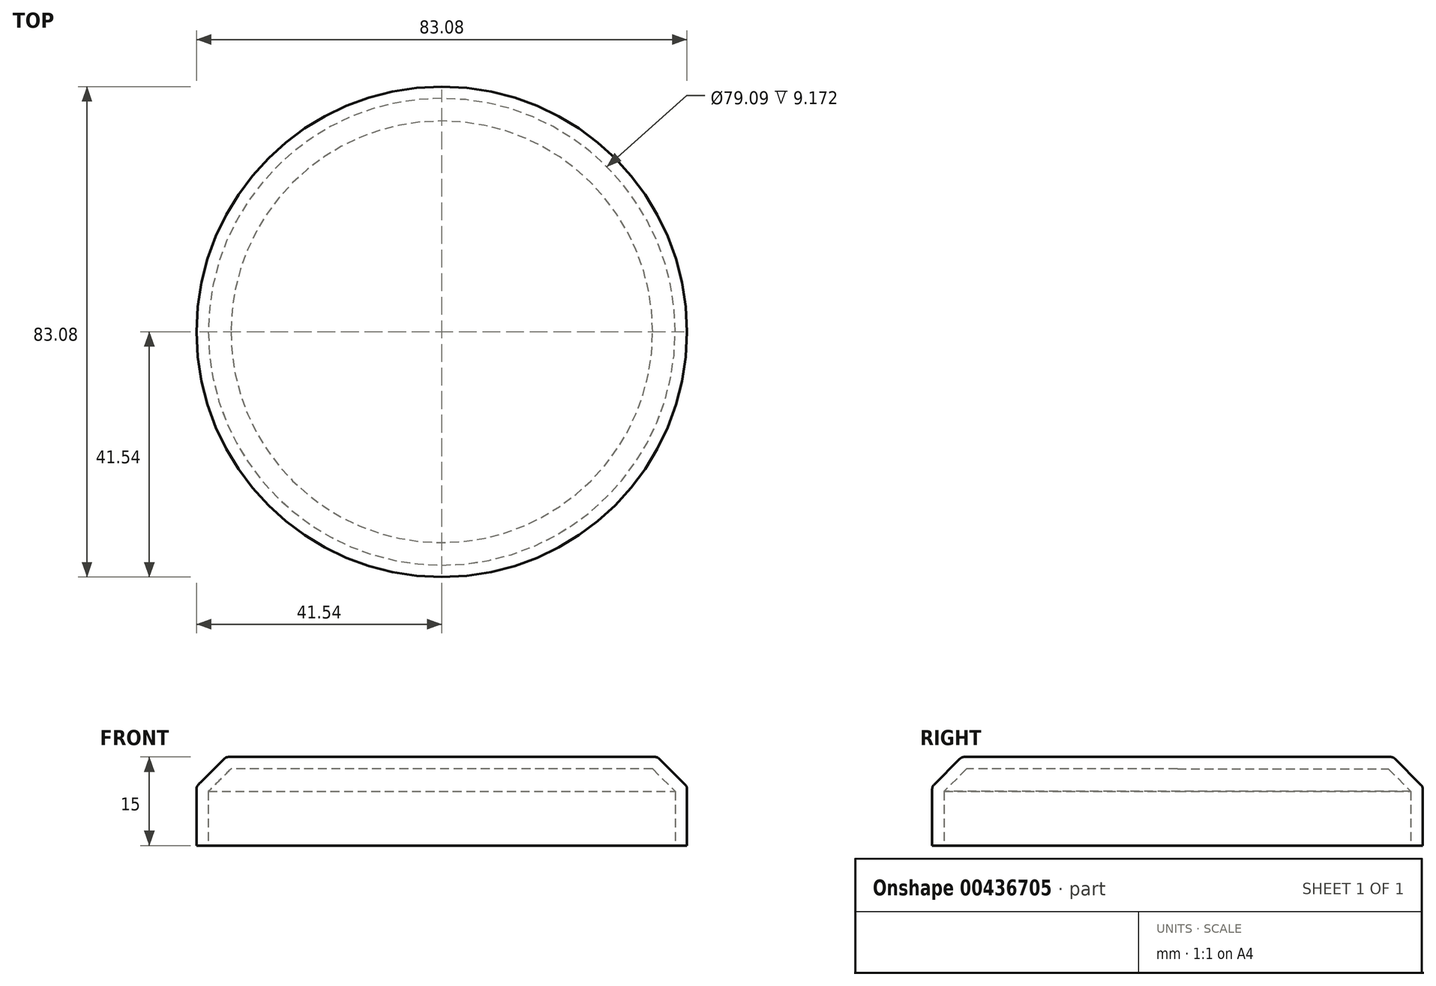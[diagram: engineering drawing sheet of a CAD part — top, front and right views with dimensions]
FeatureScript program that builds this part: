
annotation { "Feature Type Name" : "Feature", "Feature Type Description" : "" }
export const myFeature = defineFeature(function(context is Context, id is Id, definition is map)
    precondition{}
    {
        {
            var Q0;
            Q0=qCreatedBy(makeId("Top.planeOp"),FACE);
            var sketch = newSketch(context, id + "F0", { "sketchPlane" : qUnion([Q0])});
            skCircle(sketch, "E0", {"center": v(0, 0) * mm, "radius": 41.54 * mm});
            skSolve(sketch);
        }
        {
            var Q0;
            Q0 = qSketchRegion(id + "F0", true);
            extrude(context, id + "F1", {"entities" : qUnion([Q0]), "depth" : 15 * mm});
        }
        {
            var Q0;
            Q0=makeQuery(id+"F1.opExtrude","CAP_EDGE",EDGE,{"disambiguationData":[OSD([sQuery(id+"F0.wireOp",EDGE,"E0")])],"isStart":false});
            chamfer(context, id + "F2", {"entities" : qUnion([Q0]), "width" : 5 * mm, "tangentPropagation" : true});
        }
        {
            var Q0;
            Q0=makeQuery(id+"F1.opExtrude","CAP_FACE",FACE,{"disambiguationData":[OSD([sQuery(id+"F0.wireOp",EDGE,"E0")])],"isStart":true});
            shell(context, id + "F3", {"entities" : qUnion([Q0]), "thickness" : 2 * mm});
        }
        {
            var Q0;
            Q0=makeQuery(id+"F2.opChamfer","BLEND_FACE",FACE,{"disambiguationData":[OSD([sQuery(id+"F0.wireOp",EDGE,"E0")])]});
            fillet(context, id + "F4", {"entities" : qUnion([Q0]), "radius" : 1 * mm, "tangentPropagation" : true, "allowEdgeOverflow" : false});
        }
    });
